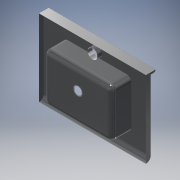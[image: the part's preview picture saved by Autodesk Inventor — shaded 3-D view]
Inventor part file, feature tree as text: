
AUTODESK INVENTOR PART (.ipt)
format: ipt  version: 2016 (Build 200138000, 138)  size: 372,224 bytes
history: native  units: mm
features: sketch x19, extrude x7, revolve x4, sweep x4, other x1, fillet x1, shell x1
ambient origin geometry x8: Origin, YZ Plane, XZ Plane, XY Plane, X Axis, Y Axis, Z Axis, Center Point
bodies: Body1 (feature_tree)
feature tree (37):
  other  "Sólido1"
  sketch  "Boceto1"  dims[d2=700.0mm d3=500.0mm]
  extrude  "Extrusión1"  Depth=500.0mm
  revolve  "Revolución1"  [1 undecoded]
  revolve  "Revolución2"  Angle=90.0deg
  revolve  "Revolución3"  Angle=90.0deg
  revolve  "Revolución4"  [1 undecoded]
  extrude  "Extrusión2"  TaperAngle=0.0deg  [1 undecoded]
  sweep  "Barrido1"
  sweep  "Barrido2"
  sweep  "Barrido3"
  sweep  "Barrido4"
  extrude  "Extrusión3"  Depth=50.0mm
  extrude  "Extrusión4"  Depth=50.0mm
  extrude  "Extrusión6"  Depth=20.0mm
  fillet  "Fillet1"  Radius=20.0mm
  extrude  "Extrusion11"  Depth=100.0mm
  extrude  "Extrusion12"  Depth=10.0mm TaperAngle=0.0deg
  shell  "Shell1"  Thickness=1.0mm
  sketch  "Boceto3"  dims[d13=90.0deg d14=90.0deg]
  sketch  "Boceto4"  dims[d18=0.0mm d19=0.0mm]
  sketch  "Boceto5"  dims[d22=80.0mm d23=10.0mm d24=0.0mm]
  sketch  "Boceto6"  dims[d25=100.0mm d26=3.0mm d27=0.0mm]
  sketch  "Boceto7"  dims[d29=0.0mm d30=0.0mm d31=0.0mm d32=0.0mm d41=700.0mm]
  sketch  "Boceto8"  dims[d42=500.0mm d43=50.0mm]
  sketch  "Boceto 3D1"  dims[d4=2.0mm d5=50.0mm]
  sketch  "Boceto9"  dims[d44=50.0mm d45=0.0mm d67=50.0mm]
  sketch  "Boceto 3D2"  dims[d10=150.0mm d11=0.0mm d12=90.0deg]
  sketch  "Boceto10"  dims[d71=101.6mm d72=255.0mm d73=20.0mm d74=0.0mm]
  sketch  "Boceto 3D3"  dims[d15=90.0deg d16=400.0mm d17=0.0mm]
  sketch  "Boceto11"  dims[d75=20.0mm d76=100.0mm]
  sketch  "Boceto 3D4"  dims[d20=0.0mm d21=0.0mm]
  sketch  "Boceto12"  dims[d77=20.0mm d78=10.0mm d79=0.0mm d80=1.0mm]
  sketch  "Boceto13"  dims[d81=200.0mm]
  sketch  "Boceto15"  dims[d82=350.0mm]
  sketch  "Sketch21"
  sketch  "Sketch22"
note: 3 required parameter values undecoded (feature->parameter linkage not recoverable at this tier; creation-order binding heuristic only, values carry confidence <= 0.55)